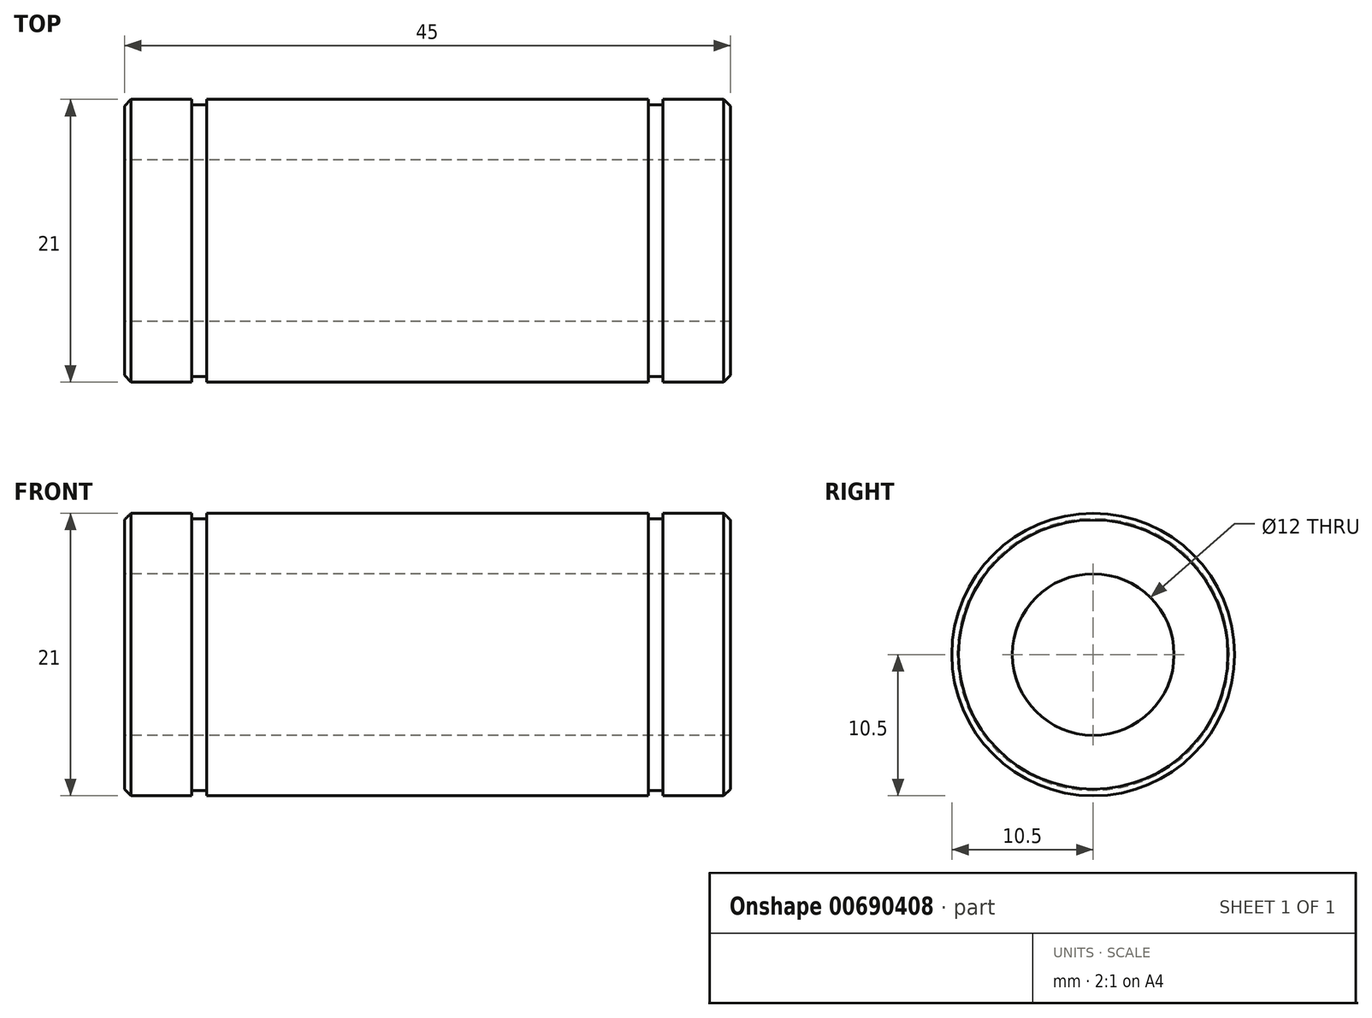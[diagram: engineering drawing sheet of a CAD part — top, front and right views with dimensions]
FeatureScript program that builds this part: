
annotation { "Feature Type Name" : "Feature", "Feature Type Description" : "" }
export const myFeature = defineFeature(function(context is Context, id is Id, definition is map)
    precondition{}
    {
        {
            var Q0;
            Q0=qCreatedBy(makeId("Front.planeOp"),FACE);
            var sketch = newSketch(context, id + "F0", { "sketchPlane" : qUnion([Q0])});
            skLineSegment(sketch, "E0", {"start": v(0, 10.5) * mm, "end": v(0, 6) * mm, "construction": true});
            skLineSegment(sketch, "E1", {"start": v(0, 6) * mm, "end": v(22.5, 6) * mm});
            skLineSegment(sketch, "E2", {"start": v(22.5, 6) * mm, "end": v(22.5, 10.5) * mm});
            skLineSegment(sketch, "E3", {"start": v(22.5, 10.5) * mm, "end": v(17.5, 10.5) * mm});
            skLineSegment(sketch, "E4", {"start": v(17.5, 10.5) * mm, "end": v(17.5, 10.1) * mm});
            skLineSegment(sketch, "E5", {"start": v(17.5, 10.1) * mm, "end": v(16.4, 10.1) * mm});
            skLineSegment(sketch, "E6", {"start": v(16.4, 10.1) * mm, "end": v(16.4, 10.5) * mm});
            skLineSegment(sketch, "E7", {"start": v(16.4, 10.5) * mm, "end": v(0, 10.5) * mm});
            skLineSegment(sketch, "E8", {"start": v(0, 0) * mm, "end": v(20.32, 0) * mm, "construction": true});
            skLineSegment(sketch, "E9.MirrorCS", {"start": v(-16.4, 10.5) * mm, "end": v(0, 10.5) * mm});
            skLineSegment(sketch, "E10.MirrorCS", {"start": v(-16.4, 10.1) * mm, "end": v(-16.4, 10.5) * mm});
            skLineSegment(sketch, "E11.MirrorCS", {"start": v(-17.5, 10.1) * mm, "end": v(-16.4, 10.1) * mm});
            skLineSegment(sketch, "E12.MirrorCS", {"start": v(-17.5, 10.5) * mm, "end": v(-17.5, 10.1) * mm});
            skLineSegment(sketch, "E13.MirrorCS", {"start": v(-22.5, 10.5) * mm, "end": v(-17.5, 10.5) * mm});
            skLineSegment(sketch, "E14.MirrorCS", {"start": v(-22.5, 6) * mm, "end": v(-22.5, 10.5) * mm});
            skLineSegment(sketch, "E15.MirrorCS", {"start": v(0, 6) * mm, "end": v(-22.5, 6) * mm});
            skSolve(sketch);
        }
        {
            var Q0;
            Q0 = qSketchRegion(id + "F0", true);
            var Q1;
            Q1=sQuery(id+"F0.wireOp",EDGE,"E8");
            revolve(context, id + "F1", {"entities" : qUnion([Q0]), "axis" : qUnion([Q1]), "revolveType" : RevolveType.FULL});
        }
        {
            var Q0;
            Q0=makeQuery(id+"F1.opRevolve","SWEPT_EDGE",EDGE,{"disambiguationData":[OSD([sQuery(id+"F0.wireOp",EDGE,"E2"),sQuery(id+"F0.wireOp",EDGE,"E3")])]});
            var Q1;
            Q1=makeQuery(id+"F1.opRevolve","SWEPT_EDGE",EDGE,{"disambiguationData":[OSD([sQuery(id+"F0.wireOp",EDGE,"E13.MirrorCS"),sQuery(id+"F0.wireOp",EDGE,"E14.MirrorCS")])]});
            chamfer(context, id + "F2", {"entities" : qUnion([Q0, Q1]), "width" : 0.5 * mm, "tangentPropagation" : true});
        }
    });
